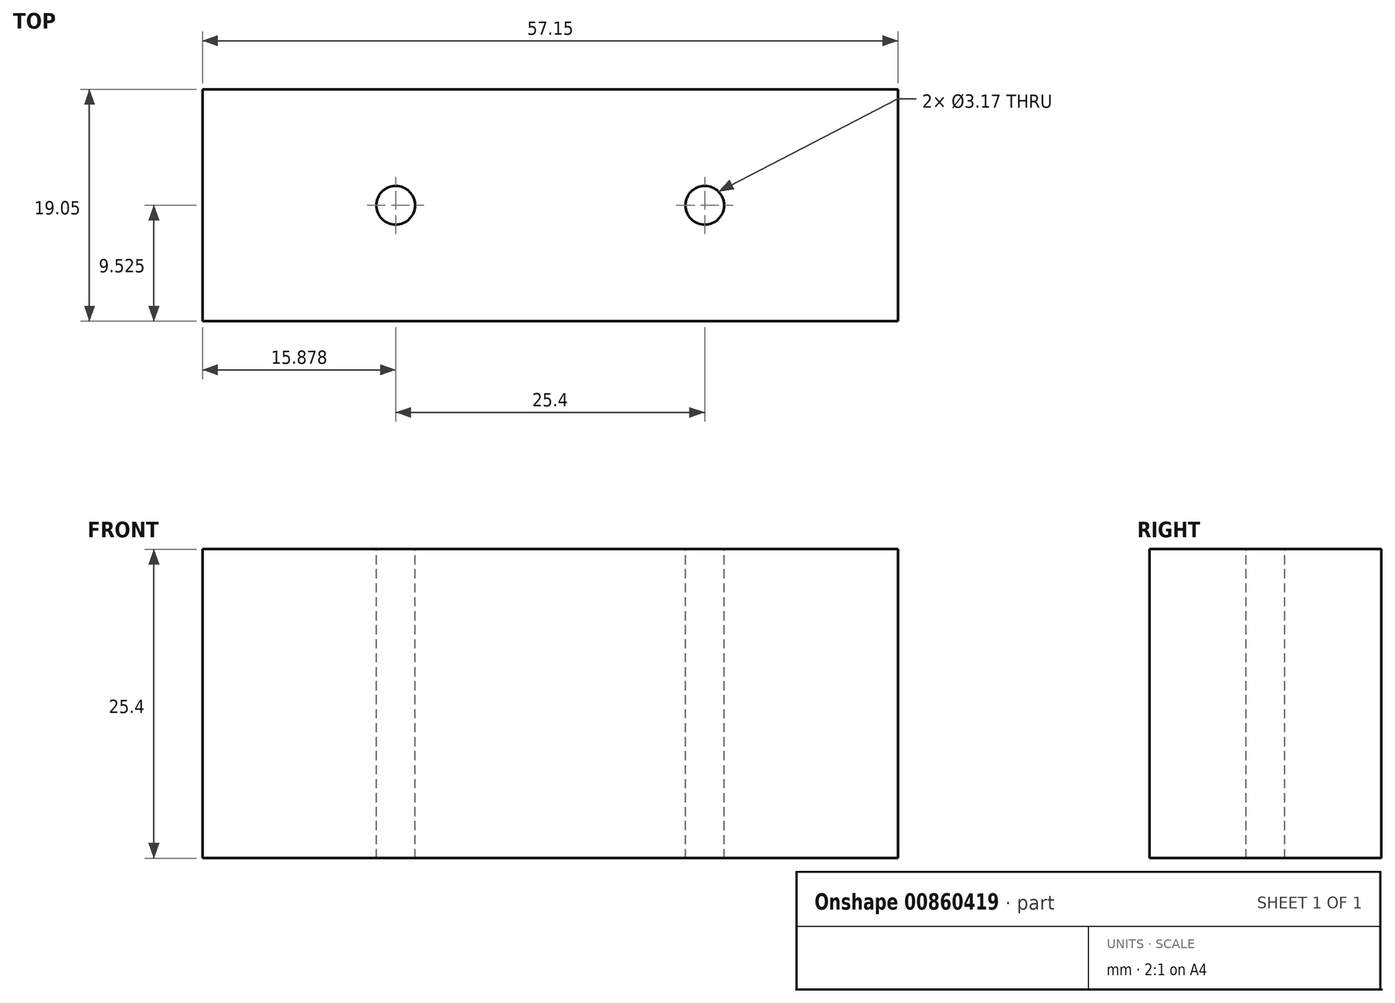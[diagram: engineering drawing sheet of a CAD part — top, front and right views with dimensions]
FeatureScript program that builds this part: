
annotation { "Feature Type Name" : "Feature", "Feature Type Description" : "" }
export const myFeature = defineFeature(function(context is Context, id is Id, definition is map)
    precondition{}
    {
        {
            var Q0;
            Q0=qCreatedBy(makeId("Front.planeOp"),FACE);
            var sketch = newSketch(context, id + "F0", { "sketchPlane" : qUnion([Q0])});
            skLineSegment(sketch, "E0.bottom", {"start": v(-124.43, 29.56) * mm, "end": v(-67.28, 29.56) * mm});
            skLineSegment(sketch, "E0.top", {"start": v(-124.43, 4.16) * mm, "end": v(-67.28, 4.16) * mm});
            skLineSegment(sketch, "E0.left", {"start": v(-124.43, 29.56) * mm, "end": v(-124.43, 4.16) * mm});
            skLineSegment(sketch, "E0.right", {"start": v(-67.28, 29.56) * mm, "end": v(-67.28, 4.16) * mm});
            skSolve(sketch);
        }
        {
            var Q0;
            Q0=makeQuery(id+"F0.imprint","IMPRINT",FACE,{"disambiguationData":[TD([[makeQuery(id+"F0.imprint","IMPRINT",EDGE,{"derivedFrom":sQuery(id+"F0.wireOp",EDGE,"E0.bottom")}),-1.0]])]});
            extrude(context, id + "F1", {"entities" : qUnion([Q0]), "depth" : 19.05 * mm, "offsetDistance" : 25.4 * mm});
        }
        {
            var Q0;
            Q0=makeQuery(id+"F1.opExtrude","SWEPT_FACE",FACE,{"disambiguationData":[OSD([sQuery(id+"F0.wireOp",EDGE,"E0.bottom")])]});
            var sketch = newSketch(context, id + "F2", { "sketchPlane" : qUnion([Q0])});
            skPoint(sketch, "E1", {"position": v(-108.55, -9.53) * mm});
            skPoint(sketch, "E2", {"position": v(-83.15, -9.53) * mm});
            skSolve(sketch);
        }
        {
            var Q0;
            Q0=sQuery(id+"F2.wireOp",VERTEX,"E1");
            var Q1;
            Q1=sQuery(id+"F2.wireOp",VERTEX,"E2");
            var Q2;
            Q2=makeQuery(id+"F1.opExtrude","SWEPT_BODY",BODY,{"disambiguationData":[OSD([sQuery(id+"F0.wireOp",EDGE,"E0.bottom"),sQuery(id+"F0.wireOp",EDGE,"E0.top"),sQuery(id+"F0.wireOp",EDGE,"E0.left"),sQuery(id+"F0.wireOp",EDGE,"E0.right")])]});
            hole(context, id + "F3", {"style" : HoleStyle.SIMPLE, "endStyle" : HoleEndStyle.THROUGH, "holeDiameter" : 3.17 * mm, "majorDiameter" : 6.35 * mm, "isTappedThrough" : true, "tappedDepth" : 12.7 * mm, "tapClearance" : 3, "locations" : qUnion([Q0, Q1]), "scope" : qUnion([Q2])});
        }
    });
